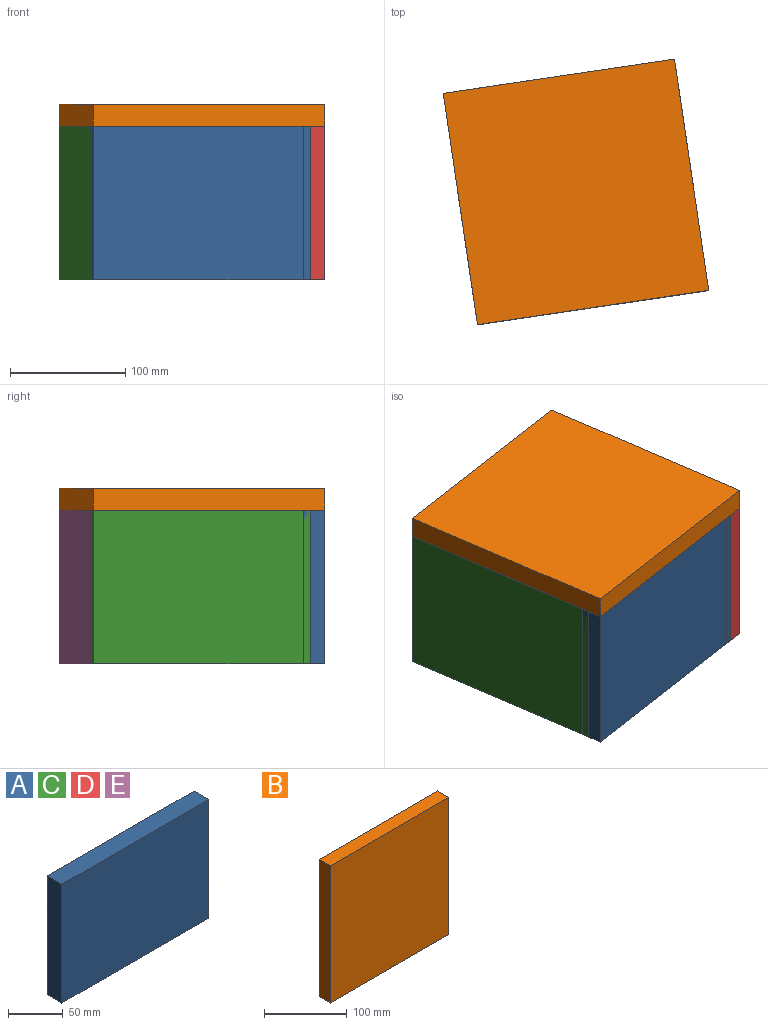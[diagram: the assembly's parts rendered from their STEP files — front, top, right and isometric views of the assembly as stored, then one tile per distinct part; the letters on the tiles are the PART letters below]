
ASSEMBLY  parts=5 mates=6
PART A: 6 faces, bbox 190.5x19.1x133.4 mm
  f0: plane 190.5x19.05mm, normal (0,0,1), area 3629mm2, adj f1,f3,f4,f5
  f1: plane 133.35x19.05mm, normal (-1,0,0), area 2540.3mm2, adj f0,f2,f4,f5
  f2: plane 190.5x19.05mm, normal (0,0,-1), area 3629mm2, adj f1,f3,f4,f5
  f3: plane 133.35x19.05mm, normal (1,0,0), area 2540.3mm2, adj f0,f2,f4,f5
  f4: plane 190.5x133.35mm, normal (0,-1,0), area 25403.2mm2, adj f0,f1,f2,f3
  f5: plane 190.5x133.35mm, normal (0,1,0), area 25403.2mm2, adj f0,f1,f2,f3
PART B: 6 faces, bbox 203.2x19.1x203.2 mm
  f0: plane 203.2x19.05mm, normal (1,0,0), area 3871mm2, adj f1,f3,f4,f5
  f1: plane 203.2x19.05mm, normal (0,0,1), area 3871mm2, adj f0,f2,f4,f5
  f2: plane 203.2x19.05mm, normal (-1,0,0), area 3871mm2, adj f1,f3,f4,f5
  f3: plane 203.2x19.05mm, normal (0,0,-1), area 3871mm2, adj f0,f2,f4,f5
  f4: plane 203.2x203.2mm, normal (0,-1,0), area 41290.2mm2, adj f0,f1,f2,f3
  f5: plane 203.2x203.2mm, normal (0,1,0), area 41290.2mm2, adj f0,f1,f2,f3
PART C: same geometry as A
PART D: same geometry as A
PART E: same geometry as A
PLACE A rot(axis=(0,0,1),8.4deg) t=(178.86,224.14,160.55)mm
PLACE B rot(axis=(0.99,0.07,0.07),90.3deg) t=(173.05,306.73,246.27)mm
PLACE C rot(axis=(0,0,-1),81.6deg) t=(90.46,300.91,160.55)mm
PLACE D rot(axis=(0,0,-1),81.6deg) t=(274.48,315.33,160.55)mm
PLACE E rot(axis=(0,0,1),8.4deg) t=(164.44,408.16,160.55)mm
MATE fastened C.f1 <-> B.f3  axis (-0.15,0.99,0) through (57.66,392.34,227.22)mm
MATE fastened B.f4 <-> A.f0  axis (0,0,-1) through (87.43,191.34,227.22)mm
MATE fastened E.f5 <-> B.f3  axis (-0.15,0.99,0) through (258.66,422.12,227.22)mm
MATE fastened D.f1 <-> B.f3  axis (-0.15,0.99,0) through (260.53,409.55,227.22)mm
MATE fastened B.f1 <-> D.f3  axis (-0.15,0.99,0) through (288.44,221.11,227.22)mm
MATE fastened B.f4 <-> D.f0  axis (0,0,-1) through (288.44,221.11,227.22)mm
